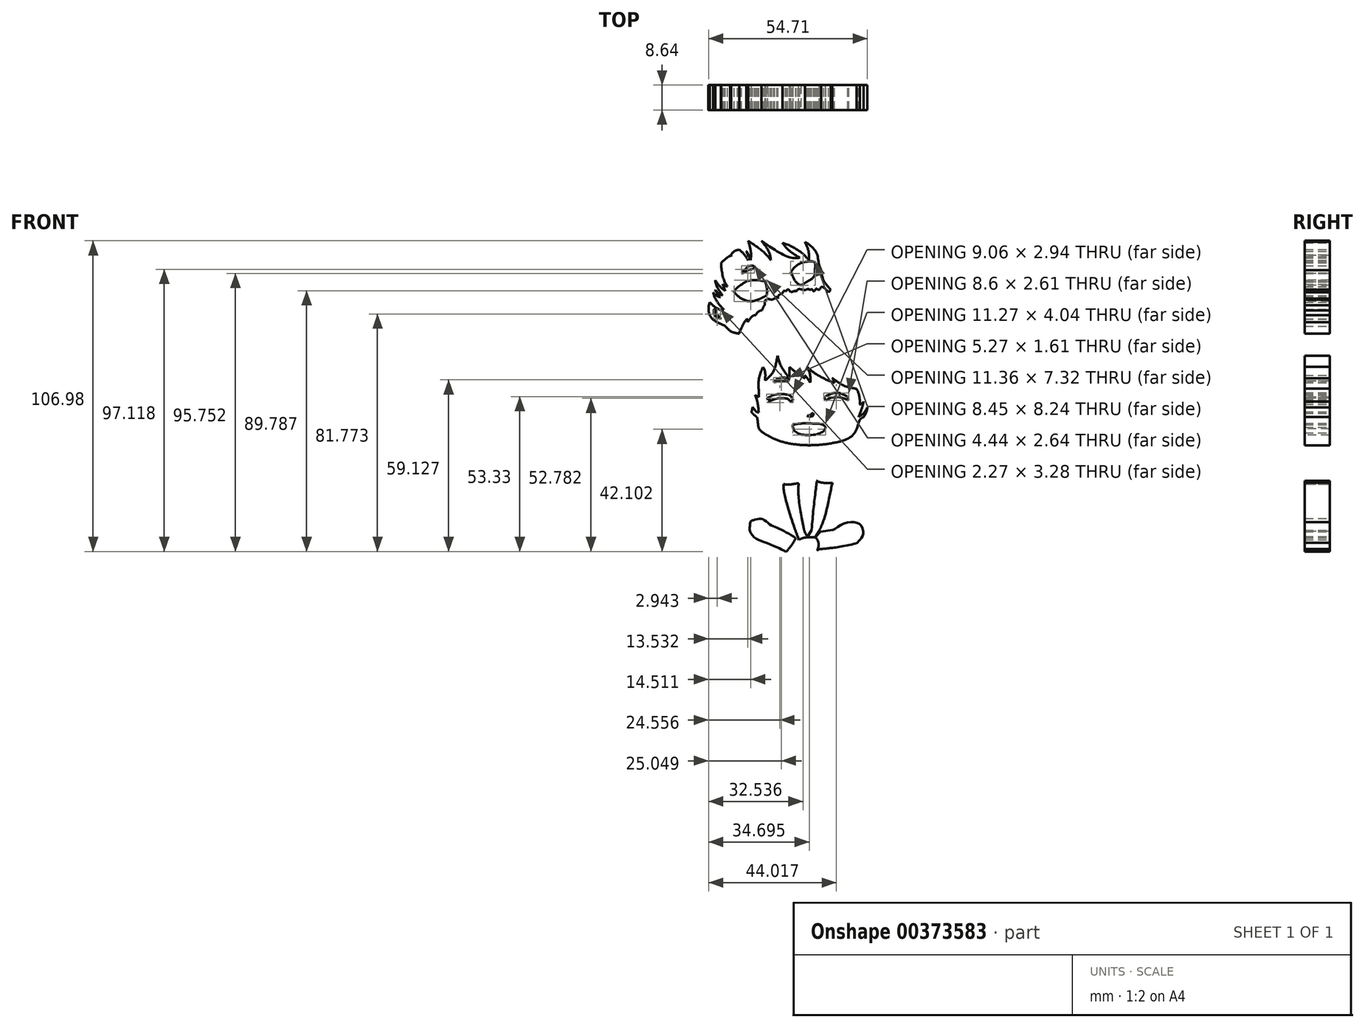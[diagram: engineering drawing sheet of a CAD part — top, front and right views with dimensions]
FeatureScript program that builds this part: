
annotation { "Feature Type Name" : "Feature", "Feature Type Description" : "" }
export const myFeature = defineFeature(function(context is Context, id is Id, definition is map)
    precondition{}
    {
        {
            var Q0;
            Q0=qCreatedBy(makeId("Front.planeOp"),FACE);
            var sketch = newSketch(context, id + "F0", { "sketchPlane" : qUnion([Q0])});
            skFitSpline(sketch, "E0", {"points": [v(-35.78, 54.46) * mm, v(-33.09, 59.85) * mm, v(-24.77, 66.06) * mm, v(-13.06, 67.81) * mm, v(-3.45, 65.7) * mm, v(-1.58, 65.82) * mm], "startDerivative": vector(10.86, 29.93) * mm, "endDerivative": vector(15.04, 3.36) * mm});
            skFitSpline(sketch, "E1", {"points": [v(-6.38, 64.18) * mm, v(-3.34, 64.3) * mm, v(-1.58, 65.82) * mm], "startDerivative": vector(6.22, -0.6) * mm, "endDerivative": vector(3.32, 3.98) * mm});
            skFitSpline(sketch, "E2", {"points": [v(-6.38, 64.18) * mm, v(-1.58, 62.66) * mm, v(2.4, 58.56) * mm, v(3.93, 55.63) * mm], "startDerivative": vector(14.2, -2.58) * mm, "endDerivative": vector(4.35, -9.84) * mm});
            skFitSpline(sketch, "E3", {"points": [v(3.93, 55.63) * mm, v(6.86, 54.23) * mm, v(8.96, 54.34) * mm], "startDerivative": vector(5.45, -3.31) * mm, "endDerivative": vector(4.6, 0.89) * mm});
            skFitSpline(sketch, "E4", {"points": [v(3.93, 54.21) * mm, v(5.68, 52.47) * mm, v(8.96, 54.34) * mm], "startDerivative": vector(3.48, -5.52) * mm, "endDerivative": vector(6.49, 5.4) * mm});
            skFitSpline(sketch, "E5", {"points": [v(5.68, 52.47) * mm, v(6.86, 48.72) * mm, v(6.86, 43.1) * mm, v(5.68, 41.7) * mm], "startDerivative": vector(3.82, -9.5) * mm, "endDerivative": vector(-5.74, -4.27) * mm});
            skFitSpline(sketch, "E6", {"points": [v(0, 51.42) * mm, v(1.35, 47.78) * mm, v(1.35, 45.1) * mm], "startDerivative": vector(3.15, -6.86) * mm, "endDerivative": vector(-0.56, -5.76) * mm});
            skFitSpline(sketch, "E7", {"points": [v(0, 51.42) * mm, v(3.93, 47.78) * mm, v(4.93, 43.33) * mm, v(5.68, 41.7) * mm], "startDerivative": vector(11.87, -7.83) * mm, "endDerivative": vector(3.7, -5.88) * mm});
            skFitSpline(sketch, "E8", {"points": [v(-7.7, 51.06) * mm, v(-5.13, 50.09) * mm, v(-0.67, 47.3) * mm, v(1.35, 45.1) * mm], "startDerivative": vector(8.03, -2.55) * mm, "endDerivative": vector(5.45, -7.1) * mm});
            skFitSpline(sketch, "E9", {"points": [v(-7.7, 51.06) * mm, v(-5.83, 48.77) * mm, v(-1.79, 45.96) * mm], "startDerivative": vector(3.67, -5.32) * mm, "endDerivative": vector(7.99, -4.9) * mm});
            skFitSpline(sketch, "E10", {"points": [v(-1.79, 45.96) * mm, v(-4.78, 45.96) * mm, v(-11.33, 49.25) * mm, v(-14.95, 51.76) * mm], "startDerivative": vector(-10.08, -1.7) * mm, "endDerivative": vector(-9.87, 7.2) * mm});
            skFitSpline(sketch, "E11", {"points": [v(-11.68, 45.1) * mm, v(-12.44, 48.14) * mm, v(-14.95, 51.76) * mm], "startDerivative": vector(-1, 6.65) * mm, "endDerivative": vector(-5.43, 6.69) * mm});
            skFitSpline(sketch, "E12", {"points": [v(-11.68, 45.1) * mm, v(-13.97, 47.7) * mm, v(-19.5, 51.76) * mm], "startDerivative": vector(-4.7, 6.12) * mm, "endDerivative": vector(-10.62, 7.16) * mm});
            skFitSpline(sketch, "E13", {"points": [v(-18.62, 45.1) * mm, v(-18.62, 48.14) * mm, v(-19.5, 51.76) * mm], "startDerivative": vector(0.4, 6.3) * mm, "endDerivative": vector(-2.13, 7.02) * mm});
            skFitSpline(sketch, "E14", {"points": [v(-20.14, 48.19) * mm, v(-19.3, 46.86) * mm, v(-18.62, 45.1) * mm], "startDerivative": vector(1.86, -2.65) * mm, "endDerivative": vector(1.2, -3.53) * mm});
            skFitSpline(sketch, "E15", {"points": [v(-22.6, 48.73) * mm, v(-20.78, 46.96) * mm, v(-19.55, 45.1) * mm], "startDerivative": vector(3.79, -3.33) * mm, "endDerivative": vector(2.3, -3.96) * mm});
            skFitSpline(sketch, "E16", {"points": [v(-20.14, 48.19) * mm, v(-19.3, 45.7) * mm, v(-19.55, 45.1) * mm], "startDerivative": vector(1.92, -4.36) * mm, "endDerivative": vector(-1.07, -1.52) * mm});
            skFitSpline(sketch, "E17", {"points": [v(-25.36, 50.22) * mm, v(-25.4, 46.4) * mm], "startDerivative": vector(-0.03, -3.81) * mm, "endDerivative": vector(-0.03, -3.81) * mm});
            skFitSpline(sketch, "E18", {"points": [v(-28.3, 48.16) * mm, v(-26.94, 47.5) * mm, v(-25.4, 46.4) * mm], "startDerivative": vector(2.87, -1.25) * mm, "endDerivative": vector(2.94, -2.24) * mm});
            skFitSpline(sketch, "E19", {"points": [v(-25.39, 47.04) * mm, v(-24.28, 48.16) * mm, v(-22.6, 48.73) * mm], "startDerivative": vector(2.06, 2.6) * mm, "endDerivative": vector(3.5, 0.8) * mm});
            skFitSpline(sketch, "E20", {"points": [v(-28.3, 48.16) * mm, v(-28.83, 43.89) * mm, v(-28.83, 43.03) * mm, v(-27.85, 38.2) * mm, v(-26.6, 36.06) * mm], "startDerivative": vector(-2.2, -17.32) * mm, "endDerivative": vector(5.7, -7.14) * mm});
            skFitSpline(sketch, "E21", {"points": [v(-28.3, 36.87) * mm, v(-27.46, 36.27) * mm, v(-26.6, 36.06) * mm], "startDerivative": vector(1.58, -1.34) * mm, "endDerivative": vector(1.82, -0.28) * mm});
            skFitSpline(sketch, "E22", {"points": [v(-30.88, 38.2) * mm, v(-29.25, 36.06) * mm, v(-27.37, 34.56) * mm], "startDerivative": vector(2.98, -4.44) * mm, "endDerivative": vector(4.04, -2.82) * mm});
            skFitSpline(sketch, "E23", {"points": [v(-28.3, 36.87) * mm, v(-27.85, 35.67) * mm, v(-27.37, 34.56) * mm], "startDerivative": vector(0.87, -2.39) * mm, "endDerivative": vector(0.98, -2.23) * mm});
            skFitSpline(sketch, "E24", {"points": [v(-30.88, 38.2) * mm, v(-30.28, 36.06) * mm, v(-28.3, 32.93) * mm], "startDerivative": vector(0.9, -4.76) * mm, "endDerivative": vector(4.12, -5.72) * mm});
            skFitSpline(sketch, "E25", {"points": [v(-30.88, 34.9) * mm, v(-29.77, 33.7) * mm, v(-28.3, 32.93) * mm], "startDerivative": vector(2.06, -2.62) * mm, "endDerivative": vector(3.1, -1.32) * mm});
            skFitSpline(sketch, "E26", {"points": [v(-30.88, 34.9) * mm, v(-30.26, 33.7) * mm, v(-29.1, 32.32) * mm], "startDerivative": vector(1.16, -2.58) * mm, "endDerivative": vector(2.37, -2.57) * mm});
            skFitSpline(sketch, "E27", {"points": [v(-31.59, 34.01) * mm, v(-30.54, 32.93) * mm, v(-29.1, 32.32) * mm], "startDerivative": vector(1.94, -2.42) * mm, "endDerivative": vector(3.02, -0.96) * mm});
            skFitSpline(sketch, "E28", {"points": [v(-31.59, 34.01) * mm, v(-30.88, 32.04) * mm, v(-29.47, 29.77) * mm, v(-27.85, 28.08) * mm], "startDerivative": vector(1.88, -6.17) * mm, "endDerivative": vector(5, -4.76) * mm});
            skFitSpline(sketch, "E29", {"points": [v(-32.7, 30.62) * mm, v(-31.27, 29.23) * mm, v(-29.1, 28.02) * mm, v(-27.85, 28.08) * mm], "startDerivative": vector(3.73, -4.02) * mm, "endDerivative": vector(4.29, 0.93) * mm});
            skFitSpline(sketch, "E30", {"points": [v(-32.7, 30.62) * mm, v(-33.17, 28.08) * mm, v(-32.15, 25.21) * mm, v(-29.1, 23.2) * mm, v(-27.37, 22.4) * mm], "startDerivative": vector(-2.96, -10.2) * mm, "endDerivative": vector(7.48, -3.45) * mm});
            skFitSpline(sketch, "E31", {"points": [v(-39.04, 37.32) * mm, v(-39.3, 32.93) * mm, v(-37.7, 28.98) * mm, v(-35.36, 26.2) * mm, v(-32.4, 23.59) * mm, v(-27.37, 22.4) * mm], "startDerivative": vector(-3.4, -21.75) * mm, "endDerivative": vector(24.84, -3.15) * mm});
            skFitSpline(sketch, "E32", {"points": [v(-39.04, 37.32) * mm, v(-39.93, 34.9) * mm, v(-41.09, 32.93) * mm], "startDerivative": vector(-1.58, -4.86) * mm, "endDerivative": vector(-2.54, -3.9) * mm});
            skFitSpline(sketch, "E33", {"points": [v(-35.78, 54.46) * mm, v(-39.04, 51.7) * mm, v(-41.02, 45.3) * mm, v(-41.02, 38.2) * mm, v(-41.09, 32.93) * mm], "startDerivative": vector(-16.55, -10.36) * mm, "endDerivative": vector(-0.72, -21.25) * mm});
            skFitSpline(sketch, "E34", {"points": [v(5.68, 41.7) * mm, v(6.42, 38.2) * mm, v(8.99, 34.9) * mm], "startDerivative": vector(0.72, -7.5) * mm, "endDerivative": vector(5.83, -6.1) * mm});
            skFitSpline(sketch, "E35", {"points": [v(8.99, 34.9) * mm, v(8.13, 34.01) * mm], "startDerivative": vector(-0.86, -0.89) * mm, "endDerivative": vector(-0.86, -0.89) * mm});
            skFitSpline(sketch, "E36", {"points": [v(-27.37, 22.4) * mm, v(-25.36, 20.57) * mm, v(-22.6, 19.8) * mm], "startDerivative": vector(3.73, -4.24) * mm, "endDerivative": vector(5.8, -0.97) * mm});
            skFitSpline(sketch, "E37", {"points": [v(-22.6, 19.8) * mm, v(-21.84, 21.8) * mm, v(-19.9, 24.77) * mm, v(-19.6, 23.8) * mm], "startDerivative": vector(1.48, 4.88) * mm, "endDerivative": vector(0.58, -6.35) * mm});
            skFitSpline(sketch, "E38", {"points": [v(-19.6, 23.8) * mm, v(-17.55, 26.1) * mm, v(-16.52, 25.98) * mm], "startDerivative": vector(3.39, 4.89) * mm, "endDerivative": vector(2.72, -1.06) * mm});
            skFitSpline(sketch, "E39", {"points": [v(-17.85, 23.8) * mm, v(-16.52, 25.98) * mm], "startDerivative": vector(1.33, 2.18) * mm, "endDerivative": vector(1.33, 2.18) * mm});
            skFitSpline(sketch, "E40", {"points": [v(-17.85, 23.8) * mm, v(-16.52, 24.3) * mm, v(-14.58, 24.3) * mm], "startDerivative": vector(2.72, 1.3) * mm, "endDerivative": vector(3.78, -0.29) * mm});
            skFitSpline(sketch, "E41", {"points": [v(-16.52, 22.4) * mm, v(-15.5, 23.24) * mm, v(-14.58, 24.3) * mm], "startDerivative": vector(2.13, 1.62) * mm, "endDerivative": vector(1.74, 2.17) * mm});
            skFitSpline(sketch, "E42", {"points": [v(-16.21, 20.46) * mm, v(-15.04, 21.35) * mm, v(-13.87, 22.8) * mm, v(-13.8, 23.8) * mm], "startDerivative": vector(3.34, 2.31) * mm, "endDerivative": vector(-0.34, 3.44) * mm});
            skFitSpline(sketch, "E43", {"points": [v(-16.52, 22.4) * mm, v(-15.73, 22.4) * mm, v(-14.58, 23.34) * mm, v(-14.38, 23.8) * mm, v(-13.8, 23.8) * mm], "startDerivative": vector(2.93, -0.64) * mm, "endDerivative": vector(3.34, -0.57) * mm});
            skFitSpline(sketch, "E44", {"points": [v(-19.6, 14.98) * mm, v(-18.89, 16.78) * mm, v(-16.52, 18.65) * mm, v(-14.58, 19.8) * mm, v(-14.58, 20.74) * mm, v(-16.21, 20.46) * mm], "startDerivative": vector(2.25, 9.04) * mm, "endDerivative": vector(-10.8, -4.04) * mm});
            skFitSpline(sketch, "E45", {"points": [v(-22.6, 19.8) * mm, v(-22.6, 18.51) * mm, v(-24.71, 14.98) * mm, v(-26.6, 12.03) * mm, v(-26.6, 10.16) * mm, v(-25.36, 7.7) * mm, v(-21.84, 8.1) * mm, v(-20.6, 12.48) * mm, v(-19.6, 14.98) * mm], "startDerivative": vector(2.63, -13.87) * mm, "endDerivative": vector(9.82, 18.02) * mm});
            skFitSpline(sketch, "E46", {"points": [v(-13.8, 37.83) * mm, v(-16.21, 38.2) * mm, v(-19.35, 38) * mm, v(-21.24, 37.1) * mm, v(-23.55, 35.39) * mm, v(-24.34, 34.01) * mm], "startDerivative": vector(-11.21, 2.22) * mm, "endDerivative": vector(-3.42, -8.47) * mm});
            skFitSpline(sketch, "E47", {"points": [v(-24.34, 34.01) * mm, v(-23.68, 33.33) * mm, v(-23.2, 32.93) * mm], "startDerivative": vector(1.23, -1.34) * mm, "endDerivative": vector(1.03, -0.8) * mm});
            skFitSpline(sketch, "E48", {"points": [v(-13.8, 37.83) * mm, v(-13.43, 37.6) * mm], "startDerivative": vector(0.37, -0.23) * mm, "endDerivative": vector(0.37, -0.23) * mm});
            skFitSpline(sketch, "E49", {"points": [v(-23.2, 32.93) * mm, v(-22.84, 33.82) * mm, v(-21.55, 35.3) * mm, v(-18.85, 36.72) * mm, v(-17.55, 37.26) * mm, v(-14.32, 37.51) * mm, v(-13.43, 37.6) * mm], "startDerivative": vector(2.32, 7) * mm, "endDerivative": vector(5.9, 0.82) * mm});
            skFitSpline(sketch, "E50", {"points": [v(-23.2, 32.93) * mm, v(-22.16, 32.07) * mm, v(-20.07, 31.13) * mm, v(-17.58, 31.02) * mm, v(-13.18, 32.93) * mm], "startDerivative": vector(5.1, -4.84) * mm, "endDerivative": vector(13.78, 7.2) * mm});
            skFitSpline(sketch, "E51", {"points": [v(-13.18, 32.93) * mm, v(-12.97, 34.38) * mm, v(-13.18, 36.06) * mm, v(-13.43, 37.05) * mm, v(-13.73, 37.56) * mm], "startDerivative": vector(1.07, 4.96) * mm, "endDerivative": vector(-1.82, 2.61) * mm});
            skFitSpline(sketch, "E52", {"points": [v(-16.59, 31.32) * mm, v(-17.53, 31.95) * mm, v(-18.37, 33.45) * mm, v(-18.45, 35.12) * mm, v(-17.58, 36.38) * mm, v(-16.01, 36.66) * mm, v(-14.94, 36.4) * mm, v(-14.2, 35.1) * mm, v(-14.22, 32.93) * mm, v(-14.33, 32.34) * mm], "startDerivative": vector(-9.83, 5) * mm, "endDerivative": vector(-1.64, -6.43) * mm});
            skFitSpline(sketch, "E53", {"points": [v(-17.58, 34.3) * mm, v(-17.55, 33.82) * mm, v(-17.21, 33.22) * mm, v(-16.8, 33.82) * mm, v(-16.46, 34.13) * mm, v(-16.42, 35.27) * mm, v(-16.8, 35.7) * mm, v(-17.55, 35.46) * mm, v(-17.79, 34.9) * mm, v(-17.75, 34.54) * mm, v(-17.58, 34.3) * mm]});
            skFitSpline(sketch, "E54", {"points": [v(-14.94, 34.22) * mm, v(-14.62, 34.17) * mm, v(-14.56, 33.22) * mm, v(-15, 33.22) * mm, v(-15.46, 33.22) * mm, v(-15.78, 33.22) * mm, v(-16, 33.45) * mm, v(-15.29, 33.53) * mm, v(-14.99, 33.82) * mm, v(-14.94, 34.22) * mm]});
            skFitSpline(sketch, "E55", {"points": [v(-21.86, 40.58) * mm, v(-20.54, 42) * mm, v(-19.37, 43) * mm, v(-17.81, 43.17) * mm, v(-17.4, 42.76) * mm, v(-17.79, 42.15) * mm, v(-19.19, 41.75) * mm, v(-20.51, 41.11) * mm, v(-21.86, 40.58) * mm]});
            skFitSpline(sketch, "E56", {"points": [v(-30.97, 28.2) * mm, v(-31.3, 28.04) * mm, v(-31.35, 27.36) * mm, v(-31.27, 26.59) * mm, v(-30.7, 25.8) * mm, v(-29.36, 25) * mm, v(-29.04, 24.94) * mm, v(-29.2, 25.39) * mm, v(-29.7, 25.86) * mm, v(-30.46, 26.52) * mm, v(-30.7, 26.9) * mm, v(-30.82, 27.76) * mm, v(-30.97, 28.2) * mm]});
            skFitSpline(sketch, "E57", {"points": [v(-28.79, 44.25) * mm, v(-27.31, 45.49) * mm, v(-25.77, 46.69) * mm], "startDerivative": vector(2.92, 2.5) * mm, "endDerivative": vector(3.1, 2.35) * mm});
            skFitSpline(sketch, "E58", {"points": [v(-23.28, 7.38) * mm, v(-23.34, 3.18) * mm, v(-22.86, 0) * mm, v(-22.26, -2.26) * mm, v(-22.26, -4.08) * mm, v(-21.65, -3.47) * mm, v(-20.8, -2.26) * mm], "startDerivative": vector(-0.82, -18.5) * mm, "endDerivative": vector(5.85, 8.57) * mm});
            skFitSpline(sketch, "E59", {"points": [v(-20.8, -2.26) * mm, v(-19.94, -4.93) * mm, v(-18.82, -7.88) * mm], "startDerivative": vector(1.69, -5.44) * mm, "endDerivative": vector(2.28, -5.8) * mm});
            skFitSpline(sketch, "E60", {"points": [v(-18.82, -7.88) * mm, v(-18.2, -6.6) * mm, v(-18, -5.44) * mm], "startDerivative": vector(1.37, 2.44) * mm, "endDerivative": vector(0.25, 2.45) * mm});
            skFitSpline(sketch, "E61", {"points": [v(-18, -5.44) * mm, v(-16.63, -7.12) * mm, v(-15.87, -7.32) * mm], "startDerivative": vector(2.26, -3.36) * mm, "endDerivative": vector(2, -0.14) * mm});
            skFitSpline(sketch, "E62", {"points": [v(-17.14, -1.42) * mm, v(-16.38, -3.5) * mm, v(-15.87, -7.32) * mm], "startDerivative": vector(1.96, -4.43) * mm, "endDerivative": vector(0.65, -7.25) * mm});
            skFitSpline(sketch, "E63", {"points": [v(-17.14, -1.42) * mm, v(-15.87, -2.06) * mm], "startDerivative": vector(1.27, -0.64) * mm, "endDerivative": vector(1.27, -0.64) * mm});
            skFitSpline(sketch, "E64", {"points": [v(-14.4, 8.3) * mm, v(-15.2, 6.36) * mm, v(-15.87, 3.77) * mm, v(-15.87, 0) * mm, v(-15.87, -2.06) * mm], "startDerivative": vector(-3.72, -8.42) * mm, "endDerivative": vector(-0.16, -8.38) * mm});
            skFitSpline(sketch, "E65", {"points": [v(-14.4, 8.3) * mm, v(-13.73, 6.87) * mm, v(-13.68, 3.62) * mm], "startDerivative": vector(1.93, -3.06) * mm, "endDerivative": vector(-0.36, -6.12) * mm});
            skFitSpline(sketch, "E66", {"points": [v(-9.36, 12.16) * mm, v(-9.97, 9.37) * mm, v(-11.09, 6.36) * mm, v(-13.68, 3.62) * mm], "startDerivative": vector(-1.82, -8.85) * mm, "endDerivative": vector(-8.2, -7.26) * mm});
            skFitSpline(sketch, "E67", {"points": [v(-9.36, 12.16) * mm, v(-8.44, 9.15) * mm, v(-6.35, 5.84) * mm, v(-5.23, 4.47) * mm], "startDerivative": vector(1.84, -8.43) * mm, "endDerivative": vector(3.88, -4.54) * mm});
            skFitSpline(sketch, "E68", {"points": [v(-5.23, 8.3) * mm, v(-5.23, 4.47) * mm], "startDerivative": vector(0, -3.83) * mm, "endDerivative": vector(0, -3.83) * mm});
            skFitSpline(sketch, "E69", {"points": [v(-5.23, 8.3) * mm, v(-2.64, 6.14) * mm, v(0, 4.47) * mm], "startDerivative": vector(5.02, -4.43) * mm, "endDerivative": vector(5.45, -3.23) * mm});
            skFitSpline(sketch, "E70", {"points": [v(-0.65, 6.2) * mm, v(0, 5.43) * mm, v(0, 4.47) * mm], "startDerivative": vector(1.62, -1.4) * mm, "endDerivative": vector(-0.32, -2.06) * mm});
            skFitSpline(sketch, "E71", {"points": [v(0, 5.43) * mm, v(0.87, 4.47) * mm, v(1.84, 2.89) * mm], "startDerivative": vector(1.94, -1.94) * mm, "endDerivative": vector(1.74, -3.11) * mm});
            skFitSpline(sketch, "E72", {"points": [v(0.77, 8.38) * mm, v(1.53, 6.6) * mm, v(1.94, 4.47) * mm, v(1.84, 2.89) * mm], "startDerivative": vector(2.45, -5.04) * mm, "endDerivative": vector(-0.63, -4.93) * mm});
            skFitSpline(sketch, "E73", {"points": [v(0.77, 8.38) * mm, v(3.16, 6.35) * mm, v(8.35, 3.5) * mm, v(10.23, 2.89) * mm], "startDerivative": vector(6.23, -6.11) * mm, "endDerivative": vector(6.35, -1.6) * mm});
            skFitSpline(sketch, "E74", {"points": [v(8.4, 5.43) * mm, v(9.47, 4.47) * mm, v(10.23, 2.89) * mm], "startDerivative": vector(2.43, -1.8) * mm, "endDerivative": vector(1.25, -3.26) * mm});
            skFitSpline(sketch, "E75", {"points": [v(9.47, 4.47) * mm, v(11.3, 3.17) * mm, v(14.43, 1.5) * mm, v(17.76, 0.9) * mm], "startDerivative": vector(5.9, -4.32) * mm, "endDerivative": vector(9.5, -0.91) * mm});
            skFitSpline(sketch, "E76", {"points": [v(17.76, 0.9) * mm, v(18.62, -1.15) * mm, v(18.96, -4.2) * mm, v(18.83, -4.8) * mm], "startDerivative": vector(2.57, -4.83) * mm, "endDerivative": vector(-0.84, -2.34) * mm});
            skFitSpline(sketch, "E77", {"points": [v(20.29, -1.88) * mm, v(20.25, -3.6) * mm, v(18.89, -4.64) * mm], "startDerivative": vector(0.57, -3.76) * mm, "endDerivative": vector(-3.37, -1.76) * mm});
            skFitSpline(sketch, "E78", {"points": [v(20.25, -3.6) * mm, v(19.66, -5.87) * mm, v(18.54, -8.86) * mm], "startDerivative": vector(-1.1, -4.78) * mm, "endDerivative": vector(-2.28, -5.73) * mm});
            skFitSpline(sketch, "E79", {"points": [v(18.54, -8.86) * mm, v(20.25, -7.54) * mm, v(21.54, -5.65) * mm], "startDerivative": vector(3.67, 2.44) * mm, "endDerivative": vector(2.32, 3.97) * mm});
            skFitSpline(sketch, "E80", {"points": [v(20.25, -8.86) * mm, v(21.11, -7.37) * mm, v(21.54, -5.65) * mm], "startDerivative": vector(1.96, 2.91) * mm, "endDerivative": vector(0.63, 3.5) * mm});
            skFitSpline(sketch, "E81", {"points": [v(20.25, -8.86) * mm, v(21.54, -7.7) * mm, v(22.57, -4.64) * mm], "startDerivative": vector(3.33, 2.19) * mm, "endDerivative": vector(1.4, 6.06) * mm});
            skFitSpline(sketch, "E82", {"points": [v(26.04, 4.47) * mm, v(25.9, 1.67) * mm, v(24.3, -2.57) * mm, v(22.57, -4.64) * mm], "startDerivative": vector(0.27, -8.4) * mm, "endDerivative": vector(-5.95, -5.77) * mm});
            skFitSpline(sketch, "E83", {"points": [v(20.25, 23.62) * mm, v(23.8, 18.8) * mm, v(26.54, 12.9) * mm, v(27.62, 7.28) * mm, v(26.04, 4.47) * mm], "startDerivative": vector(14.13, -17.43) * mm, "endDerivative": vector(-10.63, -12.77) * mm});
            skFitSpline(sketch, "E84", {"points": [v(10.72, 30.44) * mm, v(14.03, 28.92) * mm, v(20.25, 23.62) * mm], "startDerivative": vector(7.85, -2.76) * mm, "endDerivative": vector(10.99, -10.37) * mm});
            skFitSpline(sketch, "E85", {"points": [v(-18.43, -7.16) * mm, v(-17.63, -8.03) * mm, v(-16.42, -9) * mm], "startDerivative": vector(1.6, -1.88) * mm, "endDerivative": vector(2.41, -1.8) * mm});
            skFitSpline(sketch, "E86", {"points": [v(-16.42, -9) * mm, v(-16.15, -11.08) * mm, v(-15.76, -12.96) * mm, v(-14.27, -14.41) * mm], "startDerivative": vector(0.9, -6.15) * mm, "endDerivative": vector(5.24, -3.93) * mm});
            skFitSpline(sketch, "E87", {"points": [v(-14.27, -14.41) * mm, v(-8.74, -17.13) * mm, v(0.52, -18.6) * mm, v(10.03, -17.8) * mm, v(16.3, -15.35) * mm, v(18.33, -11.69) * mm, v(18.99, -9.75) * mm, v(20.25, -8.86) * mm], "startDerivative": vector(32.62, -19.16) * mm, "endDerivative": vector(18.52, 9.45) * mm});
            skFitSpline(sketch, "E88", {"points": [v(-4.09, -11.59) * mm, v(-3.93, -13.01) * mm, v(-1.75, -14.74) * mm, v(3.5, -14.95) * mm, v(6.4, -13.78) * mm, v(7.16, -12.5) * mm], "startDerivative": vector(-0.66, -9.66) * mm, "endDerivative": vector(3.65, 8.99) * mm});
            skFitSpline(sketch, "E89", {"points": [v(-4.09, -11.59) * mm, v(-1.75, -11.18) * mm, v(2.88, -11.13) * mm, v(6.34, -11.59) * mm, v(7.16, -12.5) * mm], "startDerivative": vector(9.19, 2.09) * mm, "endDerivative": vector(3.56, -6.23) * mm});
            skFitSpline(sketch, "E90", {"points": [v(-13.14, -2.74) * mm, v(-11.16, -1.46) * mm, v(-7.19, -1) * mm, v(-4.7, -1.87) * mm, v(-4.09, -3.2) * mm], "startDerivative": vector(7.11, 5.91) * mm, "endDerivative": vector(1.95, -7.59) * mm});
            skFitSpline(sketch, "E91", {"points": [v(-12.53, -3.9) * mm, v(-10.3, -2.69) * mm, v(-6.22, -2.58) * mm, v(-4.9, -3.6) * mm], "startDerivative": vector(5.8, 4.3) * mm, "endDerivative": vector(3.8, -4.53) * mm});
            skLineSegment(sketch, "E92", {"start": v(-13.14, -2.74) * mm, "end": v(-11.9, -2.74) * mm});
            skLineSegment(sketch, "E93", {"start": v(-11.9, -2.74) * mm, "end": v(-12.53, -3.9) * mm});
            skLineSegment(sketch, "E94", {"start": v(-4.9, -3.6) * mm, "end": v(-4.09, -3.2) * mm});
            skLineSegment(sketch, "E95", {"start": v(6.55, -2.23) * mm, "end": v(7.31, -3.2) * mm});
            skFitSpline(sketch, "E96", {"points": [v(6.55, -2.23) * mm, v(8.38, -1.16) * mm, v(9.6, -0.75) * mm, v(11.79, -0.65) * mm, v(15.15, -2.23) * mm], "startDerivative": vector(8, 5.03) * mm, "endDerivative": vector(10.7, -6.4) * mm});
            skFitSpline(sketch, "E97", {"points": [v(7.31, -3.2) * mm, v(8.74, -2.4) * mm, v(11.46, -2.07) * mm, v(14.47, -2.85) * mm, v(14.97, -3.2) * mm], "startDerivative": vector(5.6, 3.74) * mm, "endDerivative": vector(2.6, -2.24) * mm});
            skLineSegment(sketch, "E98", {"start": v(14.97, -3.2) * mm, "end": v(14.75, -2.5) * mm});
            skLineSegment(sketch, "E99", {"start": v(14.75, -2.5) * mm, "end": v(15.15, -2.23) * mm});
            skFitSpline(sketch, "E100", {"points": [v(-10.76, 3.1) * mm, v(-9.28, 4.27) * mm, v(-7.37, 4.73) * mm, v(-5.92, 4.45) * mm], "startDerivative": vector(3.94, 3.8) * mm, "endDerivative": vector(4.52, -1.34) * mm});
            skFitSpline(sketch, "E101", {"points": [v(-10.76, 3.1) * mm, v(-9.5, 3.3) * mm, v(-7.58, 3.56) * mm, v(-5.72, 3.53) * mm, v(-5.46, 4.12) * mm, v(-5.92, 4.45) * mm], "startDerivative": vector(5.75, 0.81) * mm, "endDerivative": vector(-4.31, 1.76) * mm});
            skFitSpline(sketch, "E102", {"points": [v(0.85, -8.55) * mm, v(1.9, -8.23) * mm, v(2.45, -7.68) * mm, v(2.9, -7.71) * mm, v(2.7, -8.55) * mm, v(0.85, -8.55) * mm]});
            skFitSpline(sketch, "E103", {"points": [v(-2.2, -18.44) * mm, v(-1.78, -19.48) * mm, v(0, -20.69) * mm, v(0.97, -21.23) * mm, v(1, -21.96) * mm, v(1.06, -23.14) * mm, v(1.3, -23.65) * mm], "startDerivative": vector(1.27, -6.3) * mm, "endDerivative": vector(2.3, -3.66) * mm});
            skFitSpline(sketch, "E104", {"points": [v(4.57, -18.5) * mm, v(4.57, -19.45) * mm, v(4.03, -20.42) * mm, v(2.27, -20.72) * mm, v(2.03, -21.63) * mm, v(2.03, -22.14) * mm, v(1.58, -22.93) * mm, v(1.3, -23.65) * mm], "startDerivative": vector(0.44, -6.45) * mm, "endDerivative": vector(-1.58, -5.57) * mm});
            skFitSpline(sketch, "E105", {"points": [v(2.05, -21.8) * mm, v(3.03, -22.55) * mm, v(4.74, -24.36) * mm], "startDerivative": vector(2.26, -1.57) * mm, "endDerivative": vector(3.07, -3.46) * mm});
            skFitSpline(sketch, "E106", {"points": [v(4.74, -24.36) * mm, v(5.52, -22.62) * mm, v(5.96, -21.76) * mm, v(6.3, -20.28) * mm, v(6.42, -19.7) * mm], "startDerivative": vector(2.6, 6.16) * mm, "endDerivative": vector(0.63, 2.75) * mm});
            skFitSpline(sketch, "E107", {"points": [v(4.74, -18.5) * mm, v(5.46, -18.87) * mm, v(6.42, -19.7) * mm], "startDerivative": vector(1.6, -0.7) * mm, "endDerivative": vector(1.74, -1.68) * mm});
            skFitSpline(sketch, "E108", {"points": [v(-1.58, -24.52) * mm, v(-0.83, -23.1) * mm, v(0, -22.03) * mm], "startDerivative": vector(1.38, 2.82) * mm, "endDerivative": vector(1.8, 2.13) * mm});
            skFitSpline(sketch, "E109", {"points": [v(0, -22.03) * mm, v(0.3, -22.55) * mm, v(0.87, -23.26) * mm, v(1.15, -23.38) * mm], "startDerivative": vector(0.72, -1.4) * mm, "endDerivative": vector(1.1, -0.25) * mm});
            skFitSpline(sketch, "E110", {"points": [v(1.43, -23.25) * mm, v(2.06, -23.12) * mm, v(2.38, -22.67) * mm, v(2.38, -22.47) * mm, v(2.6, -22.19) * mm], "startDerivative": vector(2.17, 0.05) * mm, "endDerivative": vector(1.29, 1.29) * mm});
            skFitSpline(sketch, "E111", {"points": [v(-4.86, 40.56) * mm, v(-3.95, 42.26) * mm, v(-0.8, 44.32) * mm, v(3.03, 44.62) * mm], "startDerivative": vector(2.4, 6.38) * mm, "endDerivative": vector(10.4, -0.42) * mm});
            skFitSpline(sketch, "E112", {"points": [v(-4.86, 40.56) * mm, v(-3.1, 41.6) * mm, v(-1.1, 42.86) * mm, v(2.6, 43.35) * mm], "startDerivative": vector(6.11, 3.24) * mm, "endDerivative": vector(10.26, 0.35) * mm});
            skFitSpline(sketch, "E113", {"points": [v(3.03, 44.62) * mm, v(3.5, 44.07) * mm, v(3.5, 41.9) * mm], "startDerivative": vector(1.5, -1.14) * mm, "endDerivative": vector(-0.4, -4.04) * mm});
            skFitSpline(sketch, "E114", {"points": [v(2.6, 43.35) * mm, v(3.5, 41.9) * mm], "startDerivative": vector(0.9, -1.45) * mm, "endDerivative": vector(0.9, -1.45) * mm});
            skFitSpline(sketch, "E115", {"points": [v(3.5, 41.9) * mm, v(3.5, 40.56) * mm, v(3.03, 39.25) * mm, v(1.35, 38.03) * mm, v(-1.32, 36.41) * mm], "startDerivative": vector(0.33, -6.36) * mm, "endDerivative": vector(-8.61, -5.3) * mm});
            skFitSpline(sketch, "E116", {"points": [v(-4.58, 40.71) * mm, v(-4.26, 39.7) * mm, v(-2.91, 37.42) * mm, v(-1.32, 36.41) * mm], "startDerivative": vector(0.9, -3.44) * mm, "endDerivative": vector(4.86, -2.15) * mm});
            skFitSpline(sketch, "E117", {"points": [v(1.21, 37.95) * mm, v(1.21, 38.84) * mm, v(1.06, 40.14) * mm, v(-0.32, 41.9) * mm, v(-2.2, 41.61) * mm, v(-3.11, 40.35) * mm, v(-2.88, 38.79) * mm, v(-2, 37.6) * mm, v(-0.65, 36.82) * mm], "startDerivative": vector(-0.04, 9.15) * mm, "endDerivative": vector(11.42, -5.53) * mm});
            skFitSpline(sketch, "E118", {"points": [v(-2.1, 40.9) * mm, v(-2.5, 40.56) * mm, v(-2.48, 39.94) * mm, v(-2.23, 39.74) * mm, v(-2.03, 39) * mm, v(-1.89, 38.6) * mm, v(-1.7, 38.86) * mm, v(-1.57, 39.3) * mm, v(-1.32, 39.31) * mm, v(-1.08, 39.92) * mm, v(-1.32, 40.88) * mm, v(-2.1, 40.9) * mm]});
            skFitSpline(sketch, "E119", {"points": [v(0.34, 39.56) * mm, v(0, 39.11) * mm, v(0.23, 38.86) * mm, v(0.38, 38.45) * mm, v(0.63, 38.54) * mm, v(0.74, 39.13) * mm, v(0.34, 39.56) * mm]});
            skFitSpline(sketch, "E120", {"points": [v(-2.2, -18.44) * mm, v(-3.13, -19.15) * mm, v(-3.83, -20.06) * mm, v(-3.9, -20.48) * mm], "startDerivative": vector(-2.44, -1.65) * mm, "endDerivative": vector(0.03, -1.67) * mm});
            skFitSpline(sketch, "E121", {"points": [v(-3.9, -20.48) * mm, v(-3.2, -21.57) * mm, v(-2.56, -22.72) * mm, v(-1.58, -24.52) * mm], "startDerivative": vector(2.36, -3.57) * mm, "endDerivative": vector(2.69, -4.92) * mm});
            skFitSpline(sketch, "E122", {"points": [v(-3.88, -20.21) * mm, v(-4.72, -20.6) * mm, v(-7.43, -22.8) * mm, v(-8, -23.82) * mm], "startDerivative": vector(-2.78, -0.96) * mm, "endDerivative": vector(-1.18, -3.3) * mm});
            skFitSpline(sketch, "E123", {"points": [v(-8, -23.82) * mm, v(-8, -27.3) * mm, v(-8, -29.13) * mm, v(-8.42, -31.26) * mm], "startDerivative": vector(-0.1, -9.5) * mm, "endDerivative": vector(-1.7, -7.06) * mm});
            skFitSpline(sketch, "E124", {"points": [v(-8.42, -31.26) * mm, v(-6.64, -32.13) * mm, v(-3.28, -31.87) * mm, v(-2.13, -31.77) * mm], "startDerivative": vector(4.64, -3.44) * mm, "endDerivative": vector(3.81, 0.18) * mm});
            skFitSpline(sketch, "E125", {"points": [v(3.74, -30.6) * mm, v(4.9, -31.26) * mm, v(8.78, -31.67) * mm, v(10.5, -31.26) * mm], "startDerivative": vector(3.44, -2.62) * mm, "endDerivative": vector(4.84, 1.76) * mm});
            skFitSpline(sketch, "E126", {"points": [v(6.42, -19.7) * mm, v(7.8, -20.79) * mm, v(9.74, -22.54) * mm, v(10.32, -23.97) * mm], "startDerivative": vector(3.98, -3.17) * mm, "endDerivative": vector(1.17, -4.82) * mm});
            skFitSpline(sketch, "E127", {"points": [v(10.32, -23.97) * mm, v(10.32, -26.7) * mm, v(10.32, -29.67) * mm, v(10.5, -31.26) * mm], "startDerivative": vector(0.05, -7.4) * mm, "endDerivative": vector(0.84, -5.33) * mm});
            skFitSpline(sketch, "E128", {"points": [v(13.83, -16.79) * mm, v(14.7, -21.7) * mm, v(15.07, -25.82) * mm, v(12.53, -26.67) * mm, v(10.32, -26.7) * mm], "startDerivative": vector(2.3, -15.84) * mm, "endDerivative": vector(-10.1, 0.17) * mm});
            skFitSpline(sketch, "E129", {"points": [v(-10.6, -16.4) * mm, v(-11.07, -21.47) * mm, v(-11.2, -26.7) * mm, v(-8, -27.3) * mm], "startDerivative": vector(-0.77, -13.29) * mm, "endDerivative": vector(13.92, 0.84) * mm});
            skFitSpline(sketch, "E130", {"points": [v(-2.13, -31.77) * mm, v(-2.13, -36.55) * mm, v(-0.86, -44.6) * mm, v(0, -48.5) * mm, v(0.96, -50.07) * mm], "startDerivative": vector(-0.95, -16.69) * mm, "endDerivative": vector(6.48, -8.72) * mm});
            skFitSpline(sketch, "E131", {"points": [v(-7.28, -31.96) * mm, v(-7.23, -34.16) * mm, v(-5.3, -41.85) * mm, v(-2.33, -50.5) * mm], "startDerivative": vector(-0.57, -9.22) * mm, "endDerivative": vector(7.34, -20.39) * mm});
            skFitSpline(sketch, "E132", {"points": [v(9.52, -31.56) * mm, v(8.57, -35.71) * mm, v(7.04, -42.63) * mm, v(4.9, -48.23) * mm], "startDerivative": vector(-3.26, -13.28) * mm, "endDerivative": vector(-6.75, -15.51) * mm});
            skFitSpline(sketch, "E133", {"points": [v(4.04, -30.83) * mm, v(4.04, -31.64) * mm, v(3.31, -37.55) * mm, v(2.3, -47.93) * mm], "startDerivative": vector(0.28, -4.57) * mm, "endDerivative": vector(-1.89, -21.56) * mm});
            skFitSpline(sketch, "E134", {"points": [v(13.72, -26.54) * mm, v(13.67, -29.99) * mm, v(13.73, -35.38) * mm, v(13.92, -40.15) * mm], "startDerivative": vector(-0.25, -11.06) * mm, "endDerivative": vector(0.61, -13.46) * mm});
            skFitSpline(sketch, "E135", {"points": [v(9.34, -32.31) * mm, v(9.82, -36.87) * mm, v(10.13, -40.15) * mm, v(10.13, -41.58) * mm, v(10.88, -42.2) * mm, v(11.37, -43.38) * mm], "startDerivative": vector(1.4, -15.85) * mm, "endDerivative": vector(2.14, -8.64) * mm});
            skFitSpline(sketch, "E136", {"points": [v(-7.32, -33.12) * mm, v(-7.71, -36.2) * mm, v(-7.71, -37.77) * mm, v(-7.8, -39.1) * mm, v(-8, -39.76) * mm, v(-8, -40.9) * mm, v(-8.49, -41.8) * mm, v(-9, -42.11) * mm, v(-9.21, -43.15) * mm], "startDerivative": vector(-2.64, -16.89) * mm, "endDerivative": vector(-0.53, -10.83) * mm});
            skFitSpline(sketch, "E137", {"points": [v(-9.21, -43.15) * mm, v(-7.79, -44.39) * mm, v(-5.55, -45.6) * mm, v(-3.81, -46.34) * mm], "startDerivative": vector(4.1, -4.02) * mm, "endDerivative": vector(5.4, -2.04) * mm});
            skFitSpline(sketch, "E138", {"points": [v(-0.5, -46.61) * mm, v(0.88, -46.72) * mm, v(2.4, -46.68) * mm], "startDerivative": vector(2.8, -0.29) * mm, "endDerivative": vector(3.04, 0.15) * mm});
            skFitSpline(sketch, "E139", {"points": [v(5.86, -46) * mm, v(8.42, -45.18) * mm, v(11.37, -43.38) * mm], "startDerivative": vector(5.45, 1.34) * mm, "endDerivative": vector(5.58, 3.83) * mm});
            skFitSpline(sketch, "E140", {"points": [v(13.92, -40.15) * mm, v(10.13, -40.15) * mm], "startDerivative": vector(-3.78, 0) * mm, "endDerivative": vector(-3.78, 0) * mm});
            skFitSpline(sketch, "E141", {"points": [v(13.92, -43.38) * mm, v(13.92, -40.15) * mm], "startDerivative": vector(0, 3.22) * mm, "endDerivative": vector(0, 3.22) * mm});
            skFitSpline(sketch, "E142", {"points": [v(11.37, -43.38) * mm, v(13.92, -43.38) * mm, v(18.25, -44.44) * mm, v(20.2, -46.46) * mm, v(20.62, -50.35) * mm, v(17, -52.54) * mm, v(10.75, -53.8) * mm, v(7.9, -54.12) * mm, v(4.9, -54.42) * mm], "startDerivative": vector(22.04, 1.3) * mm, "endDerivative": vector(-27.53, -2.77) * mm});
            skFitSpline(sketch, "E143", {"points": [v(4.9, -48.23) * mm, v(3.6, -50.27) * mm], "startDerivative": vector(-1.3, -2.05) * mm, "endDerivative": vector(-1.3, -2.05) * mm});
            skFitSpline(sketch, "E144", {"points": [v(2.3, -47.93) * mm, v(0.96, -50.07) * mm], "startDerivative": vector(-1.34, -2.14) * mm, "endDerivative": vector(-1.34, -2.14) * mm});
            skFitSpline(sketch, "E145", {"points": [v(3.6, -50.27) * mm, v(5.42, -48.46) * mm], "startDerivative": vector(1.82, 1.82) * mm, "endDerivative": vector(1.82, 1.82) * mm});
            skFitSpline(sketch, "E146", {"points": [v(5.42, -48.46) * mm, v(7.7, -48.06) * mm, v(10, -47.59) * mm, v(13.36, -45.61) * mm, v(17.63, -45.22) * mm, v(19.64, -46.8) * mm, v(20.03, -49.6) * mm, v(19.2, -50.87) * mm, v(18.09, -52.2) * mm], "startDerivative": vector(19.5, 3.85) * mm, "endDerivative": vector(-11.06, -13.53) * mm});
            skFitSpline(sketch, "E147", {"points": [v(-9.21, -43.15) * mm, v(-11.52, -42.73) * mm, v(-14.56, -42.73) * mm, v(-17.14, -43.15) * mm, v(-18.5, -44.68) * mm], "startDerivative": vector(-9.17, 2.14) * mm, "endDerivative": vector(-5.04, -8) * mm});
            skFitSpline(sketch, "E148", {"points": [v(-3.13, -50.5) * mm, v(-6.67, -48.46) * mm, v(-9.87, -46.86) * mm, v(-11.89, -45.97) * mm, v(-13.9, -44.42) * mm, v(-15.65, -43.9) * mm, v(-17.8, -44.42) * mm, v(-18.5, -44.68) * mm, v(-18.89, -45.97) * mm, v(-18.95, -47.93) * mm, v(-17.4, -50.27) * mm, v(-13.57, -52.11) * mm, v(-8.32, -54.33) * mm, v(-7.3, -54.89) * mm, v(-6.3, -55.22) * mm], "startDerivative": vector(-37.34, 22.1) * mm, "endDerivative": vector(22.17, -6.3) * mm});
            skFitSpline(sketch, "E149", {"points": [v(-3.13, -50.5) * mm, v(-4.12, -52.41) * mm, v(-6.3, -55.22) * mm], "startDerivative": vector(-1.91, -4.23) * mm, "endDerivative": vector(-4.33, -5.17) * mm});
            skFitSpline(sketch, "E150", {"points": [v(3.6, -50.27) * mm, v(4.4, -51.39) * mm, v(4.7, -53.63) * mm, v(4.3, -54.72) * mm, v(4.9, -54.42) * mm], "startDerivative": vector(3.34, -3.74) * mm, "endDerivative": vector(4.67, 2.99) * mm});
            skFitSpline(sketch, "E151", {"points": [v(-3.13, -50.5) * mm, v(-1.75, -51.98) * mm, v(-0.66, -53.04) * mm], "startDerivative": vector(2.65, -2.9) * mm, "endDerivative": vector(2.3, -2.17) * mm});
            skPoint(sketch, "E152.1.internal.snap0", {"position": v(-2.98, -64.76) * mm});
            skFitSpline(sketch, "E152", {"points": [v(-6.3, -55.22) * mm, v(-2.98, -57.07) * mm], "startDerivative": vector(3.32, -1.86) * mm, "endDerivative": vector(3.32, -1.86) * mm});
            skFitSpline(sketch, "E153", {"points": [v(-2.98, -57.07) * mm, v(-2.33, -56.05) * mm], "startDerivative": vector(0.65, 1.03) * mm, "endDerivative": vector(0.65, 1.03) * mm});
            skFitSpline(sketch, "E154", {"points": [v(-0.66, -53.04) * mm, v(-1.04, -53.75) * mm], "startDerivative": vector(-0.38, -0.7) * mm, "endDerivative": vector(-0.38, -0.7) * mm});
            skFitSpline(sketch, "E155", {"points": [v(-2.33, -56.05) * mm, v(-2.98, -55.66) * mm, v(-3.13, -54.89) * mm, v(-2.73, -54.25) * mm, v(-1.64, -53.92) * mm, v(-1.04, -53.75) * mm], "startDerivative": vector(-3.88, 1.48) * mm, "endDerivative": vector(3, 0.98) * mm});
            skFitSpline(sketch, "E156", {"points": [v(-2.33, -51.37) * mm, v(-0.44, -50.5) * mm, v(2.5, -50.27) * mm, v(3.6, -50.27) * mm], "startDerivative": vector(4.88, 2.98) * mm, "endDerivative": vector(3.74, 0) * mm});
            skFitSpline(sketch, "E157", {"points": [v(0.96, -50.07) * mm, v(0.96, -50.31) * mm], "startDerivative": vector(0, -0.24) * mm, "endDerivative": vector(0, -0.24) * mm});
            skFitSpline(sketch, "E158", {"points": [v(-0.66, -53.04) * mm, v(0.96, -53.75) * mm, v(3.6, -55.22) * mm, v(3.6, -58.14) * mm, v(1.76, -60.17) * mm, v(0, -60) * mm, v(-1.87, -58.44) * mm, v(-2.98, -57.07) * mm], "startDerivative": vector(11.36, -5.5) * mm, "endDerivative": vector(-8.07, 10.6) * mm});
            skFitSpline(sketch, "E159", {"points": [v(4.3, -54.72) * mm, v(3.1, -54.72) * mm], "startDerivative": vector(-1.2, 0) * mm, "endDerivative": vector(-1.2, 0) * mm});
            skFitSpline(sketch, "E160", {"points": [v(-9.87, -27.31) * mm, v(-9.64, -30.06) * mm, v(-9.32, -35.11) * mm, v(-9.2, -39.1) * mm, v(-9.2, -40.86) * mm, v(-8.78, -41.96) * mm], "startDerivative": vector(1.1, -12.59) * mm, "endDerivative": vector(3.94, -8.02) * mm});
            skFitSpline(sketch, "E161", {"points": [v(-9.21, -39.6) * mm, v(-8, -39.76) * mm], "startDerivative": vector(1.21, -0.17) * mm, "endDerivative": vector(1.21, -0.17) * mm});
            skFitSpline(sketch, "E162", {"points": [v(-6.76, 19.07) * mm, v(-7.3, 18.18) * mm, v(-9.2, 18.38) * mm, v(-9.32, 18.88) * mm, v(-9.87, 20.62) * mm, v(-8.78, 21.27) * mm, v(-8, 22.07) * mm, v(-7.3, 21.72) * mm, v(-7.3, 20.72) * mm, v(-6.76, 19.07) * mm]});
            skFitSpline(sketch, "E163", {"points": [v(-7.3, 21.72) * mm, v(-6.3, 22.22) * mm, v(-5.23, 21.72) * mm, v(-4.52, 20.67) * mm, v(-5.23, 19.52) * mm, v(-4.67, 18.88) * mm, v(-6.8, 18.65) * mm], "startDerivative": vector(6.38, 4.7) * mm, "endDerivative": vector(-15.2, -0.03) * mm});
            skFitSpline(sketch, "E164", {"points": [v(-4.9, 21.44) * mm, v(-3.87, 22.67) * mm, v(-2.33, 22.82) * mm, v(-1.04, 22.37) * mm, v(-1.04, 20.37) * mm, v(-1.75, 19.32) * mm, v(-2.98, 19.57) * mm, v(-3.97, 18.83) * mm, v(-4.67, 18.88) * mm], "startDerivative": vector(6.56, 10.96) * mm, "endDerivative": vector(-7.83, 2.8) * mm});
            skFitSpline(sketch, "E165", {"points": [v(-0.94, 20.8) * mm, v(0.96, 19.87) * mm, v(2.6, 20.37) * mm, v(3.6, 21.32) * mm, v(3.6, 22.87) * mm, v(4.3, 23.22) * mm, v(3.6, 24.62) * mm, v(2.6, 24.87) * mm, v(1.52, 24.91) * mm, v(1.52, 25.76) * mm, v(0.52, 25.66) * mm, v(-0.66, 24.07) * mm, v(-1.75, 22.75) * mm], "startDerivative": vector(18.42, -12.7) * mm, "endDerivative": vector(-12.24, -12.87) * mm});
            skFitSpline(sketch, "E166", {"points": [v(-9.32, 18.88) * mm, v(-9.95, 18.33) * mm, v(-11.52, 18.38) * mm, v(-11.52, 18.88) * mm, v(-12.45, 18.88) * mm, v(-12.3, 20.37) * mm, v(-12.45, 21.72) * mm, v(-11, 21.72) * mm, v(-9.95, 21.17) * mm, v(-9.32, 21.02) * mm], "startDerivative": vector(-4.1, -6.34) * mm, "endDerivative": vector(7.28, -1) * mm});
            skFitSpline(sketch, "E167", {"points": [v(-12.45, 19.54) * mm, v(-13.75, 18.88) * mm, v(-15, 19.39) * mm], "startDerivative": vector(-2.55, -1.92) * mm, "endDerivative": vector(-2.56, 1.63) * mm});
            skFitSpline(sketch, "E168", {"points": [v(-12.45, 21.72) * mm, v(-13.45, 22.37) * mm, v(-14.1, 22.37) * mm], "startDerivative": vector(-1.8, 1.46) * mm, "endDerivative": vector(-1.5, -0.24) * mm});
            skFitSpline(sketch, "E169", {"points": [v(3.6, 22.87) * mm, v(4.9, 22.37) * mm, v(5.95, 23.62) * mm, v(7.9, 24.12) * mm, v(6.86, 25.41) * mm, v(6.61, 26.41) * mm, v(5.42, 27.11) * mm, v(4.3, 26.91) * mm, v(2.6, 26.26) * mm, v(2.6, 24.87) * mm], "startDerivative": vector(13.83, -9.17) * mm, "endDerivative": vector(3.72, -14.8) * mm});
            skFitSpline(sketch, "E170", {"points": [v(7.33, 24.87) * mm, v(8.46, 25.26) * mm, v(7.9, 27.06) * mm, v(7.9, 28.06) * mm, v(7.06, 28.1) * mm, v(5.95, 28) * mm, v(5.42, 27.11) * mm], "startDerivative": vector(9.25, 0.85) * mm, "endDerivative": vector(-2.49, -7.07) * mm});
            skFitSpline(sketch, "E171", {"points": [v(8.15, 26.3) * mm, v(9.26, 26.16) * mm, v(10.5, 27.56) * mm, v(10.06, 28.56) * mm, v(10.1, 29.26) * mm, v(9.26, 29.76) * mm, v(8.46, 30.06) * mm, v(7.46, 29.7) * mm, v(6.76, 28.76) * mm, v(6.32, 28.1) * mm], "startDerivative": vector(8.92, -3.87) * mm, "endDerivative": vector(-4.58, -6.2) * mm});
            skFitSpline(sketch, "E172", {"points": [v(-13.8, 23.8) * mm, v(-12.93, 25.26) * mm, v(-14.03, 26.91) * mm, v(-14.56, 26.91) * mm, v(-14.73, 27.8) * mm, v(-16.27, 27.11) * mm, v(-16.85, 26.1) * mm], "startDerivative": vector(6.96, 6.62) * mm, "endDerivative": vector(-1.96, -6.05) * mm});
            skFitSpline(sketch, "E173", {"points": [v(-16.85, 25.43) * mm, v(-16.52, 25.25) * mm, v(-16.17, 24.33) * mm], "startDerivative": vector(0.93, -0.28) * mm, "endDerivative": vector(0.47, -1.8) * mm});
            skFitSpline(sketch, "E174", {"points": [v(-13.14, 25.98) * mm, v(-11.52, 26.55) * mm, v(-11.52, 28.47) * mm, v(-11.52, 29.5) * mm, v(-12.93, 29.38) * mm, v(-13.76, 29.63) * mm, v(-14.73, 27.8) * mm], "startDerivative": vector(11.52, 1.32) * mm, "endDerivative": vector(-4.72, -13.22) * mm});
            skFitSpline(sketch, "E175", {"points": [v(-11.42, 27.11) * mm, v(-9.87, 27.8) * mm, v(-9.87, 29.18) * mm, v(-10.89, 30.07) * mm, v(-11.05, 31.14) * mm, v(-13.27, 31.55) * mm, v(-13.76, 29.63) * mm], "startDerivative": vector(10.88, 2.35) * mm, "endDerivative": vector(0.53, -13.09) * mm});
            skLineSegment(sketch, "E176", {"start": v(4.04, -30.83) * mm, "end": v(4.04, -30.82) * mm});
            skLineSegment(sketch, "E177", {"start": v(-11.44, 31.44) * mm, "end": v(-10.43, 31.84) * mm});
            skLineSegment(sketch, "E178", {"start": v(-10.43, 31.84) * mm, "end": v(-9.62, 32.65) * mm});
            skLineSegment(sketch, "E179", {"start": v(-9.62, 32.65) * mm, "end": v(-8.93, 31.14) * mm});
            skLineSegment(sketch, "E180", {"start": v(-8.93, 31.14) * mm, "end": v(-7.6, 30.17) * mm});
            skLineSegment(sketch, "E181", {"start": v(-7.6, 30.17) * mm, "end": v(-8.2, 28.85) * mm});
            skLineSegment(sketch, "E182", {"start": v(-8.2, 28.85) * mm, "end": v(-9.66, 28.41) * mm});
            skPoint(sketch, "E183.5.internal.snap0", {"position": v(-9.27, 31.9) * mm});
            skFitSpline(sketch, "E183", {"points": [v(-9.27, 31.9) * mm, v(-8.97, 33.04) * mm, v(-7.65, 33.8) * mm, v(-7.3, 34.54) * mm, v(-6.15, 33.6) * mm, v(-6.06, 31.9) * mm, v(-6.88, 30.77) * mm, v(-7.6, 30.17) * mm], "startDerivative": vector(0.05, 9.48) * mm, "endDerivative": vector(-5.81, -4.4) * mm});
            skFitSpline(sketch, "E184", {"points": [v(-6.31, 31.42) * mm, v(-5.25, 30.73) * mm, v(-4.48, 31.24) * mm, v(-3.16, 31.24) * mm, v(-2.9, 33.04) * mm, v(-3.33, 34.5) * mm, v(-4.78, 34.2) * mm, v(-5.72, 35.05) * mm, v(-6.67, 34.24) * mm], "startDerivative": vector(9.51, -9.34) * mm, "endDerivative": vector(-8.3, -11.28) * mm});
            skFitSpline(sketch, "E185", {"points": [v(-3.02, 34.1) * mm, v(-2.34, 35.05) * mm, v(-0.42, 34.88) * mm, v(0.52, 34.5) * mm, v(0, 33.5) * mm, v(0.65, 32.44) * mm, v(-1.14, 31.76) * mm, v(-2.93, 31.57) * mm], "startDerivative": vector(3.8, 9.23) * mm, "endDerivative": vector(-9.74, -0.65) * mm});
            skFitSpline(sketch, "E186", {"points": [v(0, 32) * mm, v(0.6, 31.03) * mm, v(1.5, 31.33) * mm, v(1.6, 32.35) * mm, v(2.5, 33.55) * mm, v(1.68, 34.15) * mm, v(1.5, 35.1) * mm, v(0, 34.8) * mm], "startDerivative": vector(2.92, -8.97) * mm, "endDerivative": vector(-12.08, -4.77) * mm});
            skFitSpline(sketch, "E187", {"points": [v(7.88, 29.96) * mm, v(6.68, 30.17) * mm, v(6.51, 32.31) * mm, v(7.46, 32.1) * mm, v(8.13, 34.01) * mm, v(9.68, 32.78) * mm, v(11.18, 32.18) * mm, v(10.72, 30.44) * mm, v(10.1, 29.26) * mm], "startDerivative": vector(-12.44, -2.64) * mm, "endDerivative": vector(-4.85, -8.9) * mm});
            skFitSpline(sketch, "E188", {"points": [v(6.35, 31.16) * mm, v(4.5, 31.16) * mm, v(4.25, 32.1) * mm, v(3.13, 32.61) * mm, v(3.73, 34.01) * mm, v(3.99, 35.35) * mm, v(4.8, 34.88) * mm, v(5.74, 35.86) * mm, v(8.13, 34.01) * mm], "startDerivative": vector(-17.35, -3.37) * mm, "endDerivative": vector(15.34, -17.76) * mm});
            skFitSpline(sketch, "E189", {"points": [v(3.86, 32.31) * mm, v(3.4, 31.2) * mm, v(2.75, 31.63) * mm, v(1.5, 31.33) * mm], "startDerivative": vector(-1.13, -4.65) * mm, "endDerivative": vector(-3.69, -1.82) * mm});
            skFitSpline(sketch, "E190", {"points": [v(1.57, 34.7) * mm, v(2.53, 35.05) * mm, v(3, 34.4) * mm, v(3.99, 35.35) * mm], "startDerivative": vector(3.34, 2.23) * mm, "endDerivative": vector(2.97, 4.1) * mm});
            skFitSpline(sketch, "E191", {"points": [v(-3.93, -13.01) * mm, v(-0.7, -13.01) * mm, v(3.99, -13.01) * mm, v(6.98, -12.95) * mm], "startDerivative": vector(9.57, 0.01) * mm, "endDerivative": vector(9.1, 0.25) * mm});
            skFitSpline(sketch, "E192", {"points": [v(-4.09, -12.48) * mm, v(-2.92, -11.84) * mm, v(2.05, -11.59) * mm, v(6.68, -11.84) * mm], "startDerivative": vector(4.31, 3.46) * mm, "endDerivative": vector(11.2, -0.76) * mm});
            skFitSpline(sketch, "E193", {"points": [v(-2.33, -50.5) * mm, v(-1.97, -51.15) * mm], "startDerivative": vector(0.36, -0.65) * mm, "endDerivative": vector(0.36, -0.65) * mm});
            skLineSegment(sketch, "E194", {"start": v(-16.85, 26.1) * mm, "end": v(-16.85, 26.1) * mm});
            skLineSegment(sketch, "E195", {"start": v(18.89, -4.64) * mm, "end": v(18.88, -4.64) * mm});
            skSolve(sketch);
        }
        {
            var Q0;
            {var subQ19=sQuery(id+"F0.wireOp",EDGE,"E61");Q0=makeQuery(id+"F0.imprint","IMPRINT",FACE,{"disambiguationData":[TD([[makeQuery(id+"F0.imprint","IMPRINT",EDGE,{"derivedFrom":subQ19}),-1.0]])]});}
            var Q1;
            Q1=makeQuery(id+"F0.imprint","IMPRINT",FACE,{"disambiguationData":[TD([[makeQuery(id+"F0.imprint","IMPRINT",EDGE,{"derivedFrom":sQuery(id+"F0.wireOp",EDGE,"E6")}),1.0]])]});
            var Q2;
            {var subQ3=sQuery(id+"F0.wireOp",EDGE,"E143");Q2=makeQuery(id+"F0.imprint","IMPRINT",FACE,{"disambiguationData":[TD([[makeQuery(id+"F0.imprint","IMPRINT",EDGE,{"derivedFrom":subQ3}),-1.0]])]});}
            var Q3;
            {var subQ4=sQuery(id+"F0.wireOp",EDGE,"E157");Q3=makeQuery(id+"F0.imprint","IMPRINT",FACE,{"disambiguationData":[TD([[makeQuery(id+"F0.imprint","IMPRINT",EDGE,{"derivedFrom":subQ4}),-1.0]])]});}
            var Q4;
            {var subQ2=sQuery(id+"F0.wireOp",EDGE,"E149");Q4=makeQuery(id+"F0.imprint","IMPRINT",FACE,{"disambiguationData":[TD([[makeQuery(id+"F0.imprint","IMPRINT",EDGE,{"derivedFrom":subQ2}),-1.0]])]});}
            var Q5;
            {var subQ1=sQuery(id+"F0.wireOp",EDGE,"E145");Q5=makeQuery(id+"F0.imprint","IMPRINT",FACE,{"disambiguationData":[TD([[makeQuery(id+"F0.imprint","IMPRINT",EDGE,{"derivedFrom":subQ1}),-1.0]])]});}
            extrude(context, id + "F1", {"entities" : qUnion([Q0, Q1, Q2, Q3, Q4, Q5]), "depth" : 8.64 * mm});
        }
    });
